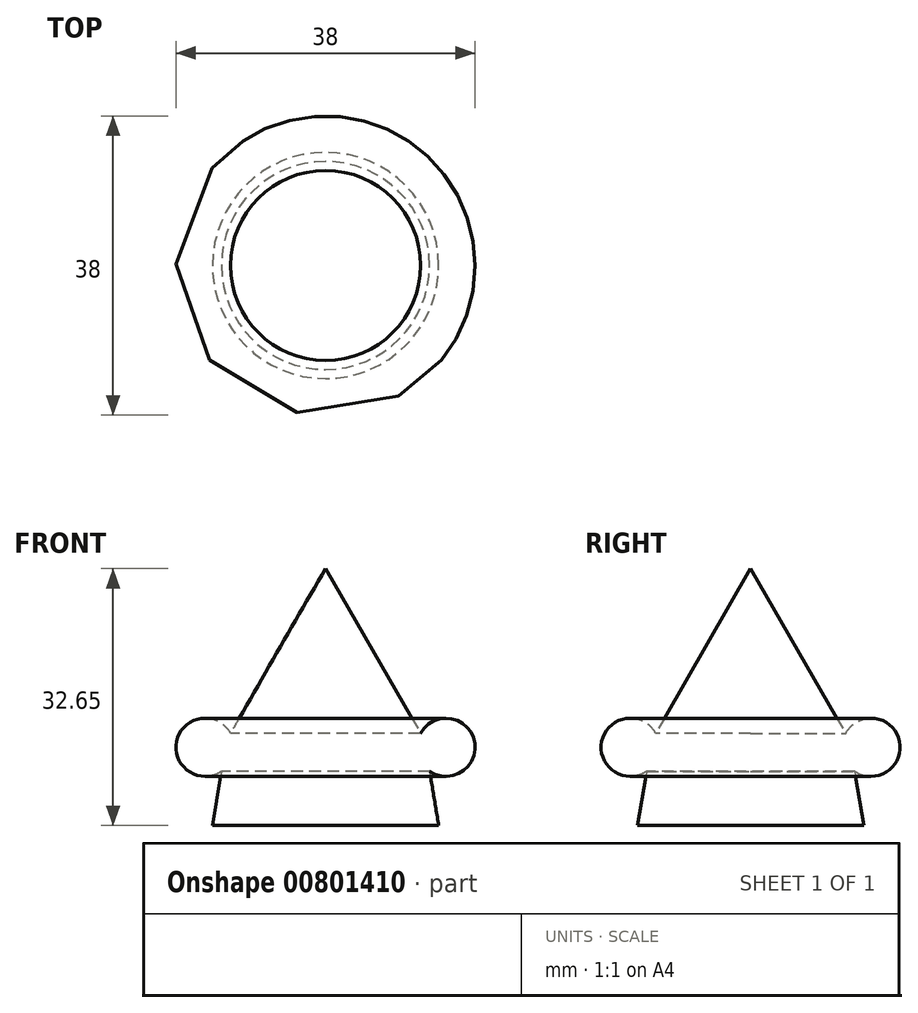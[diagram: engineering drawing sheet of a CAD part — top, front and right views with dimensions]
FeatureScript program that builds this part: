
annotation { "Feature Type Name" : "Feature", "Feature Type Description" : "" }
export const myFeature = defineFeature(function(context is Context, id is Id, definition is map)
    precondition{}
    {
        {
            var Q0;
            Q0=qCreatedBy(makeId("Front.planeOp"),FACE);
            var sketch = newSketch(context, id + "F0", { "sketchPlane" : qUnion([Q0])});
            skArc(sketch, "E0", {"start": v(13.22, 6.9) * mm, "mid": v(18.9, 10.8) * mm, "end": v(12.07, 11.73) * mm});
            skLineSegment(sketch, "E1", {"start": v(0, 0) * mm, "end": v(14.37, 0) * mm});
            skLineSegment(sketch, "E2", {"start": v(14.37, 0) * mm, "end": v(13.22, 6.9) * mm});
            skLineSegment(sketch, "E3", {"start": v(12.07, 11.73) * mm, "end": v(0, 32.65) * mm});
            skLineSegment(sketch, "E4", {"start": v(0, 32.65) * mm, "end": v(0, 0) * mm});
            skSolve(sketch);
        }
        {
            var Q0;
            Q0 = qSketchRegion(id + "F0", true);
            var Q1;
            Q1=sQuery(id+"F0.wireOp",EDGE,"E4");
            revolve(context, id + "F1", {"surfaceOperationType" : NewSurfaceOperationType.NEW, "entities" : qUnion([Q0]), "axis" : qUnion([Q1]), "revolveType" : RevolveType.FULL});
        }
    });
